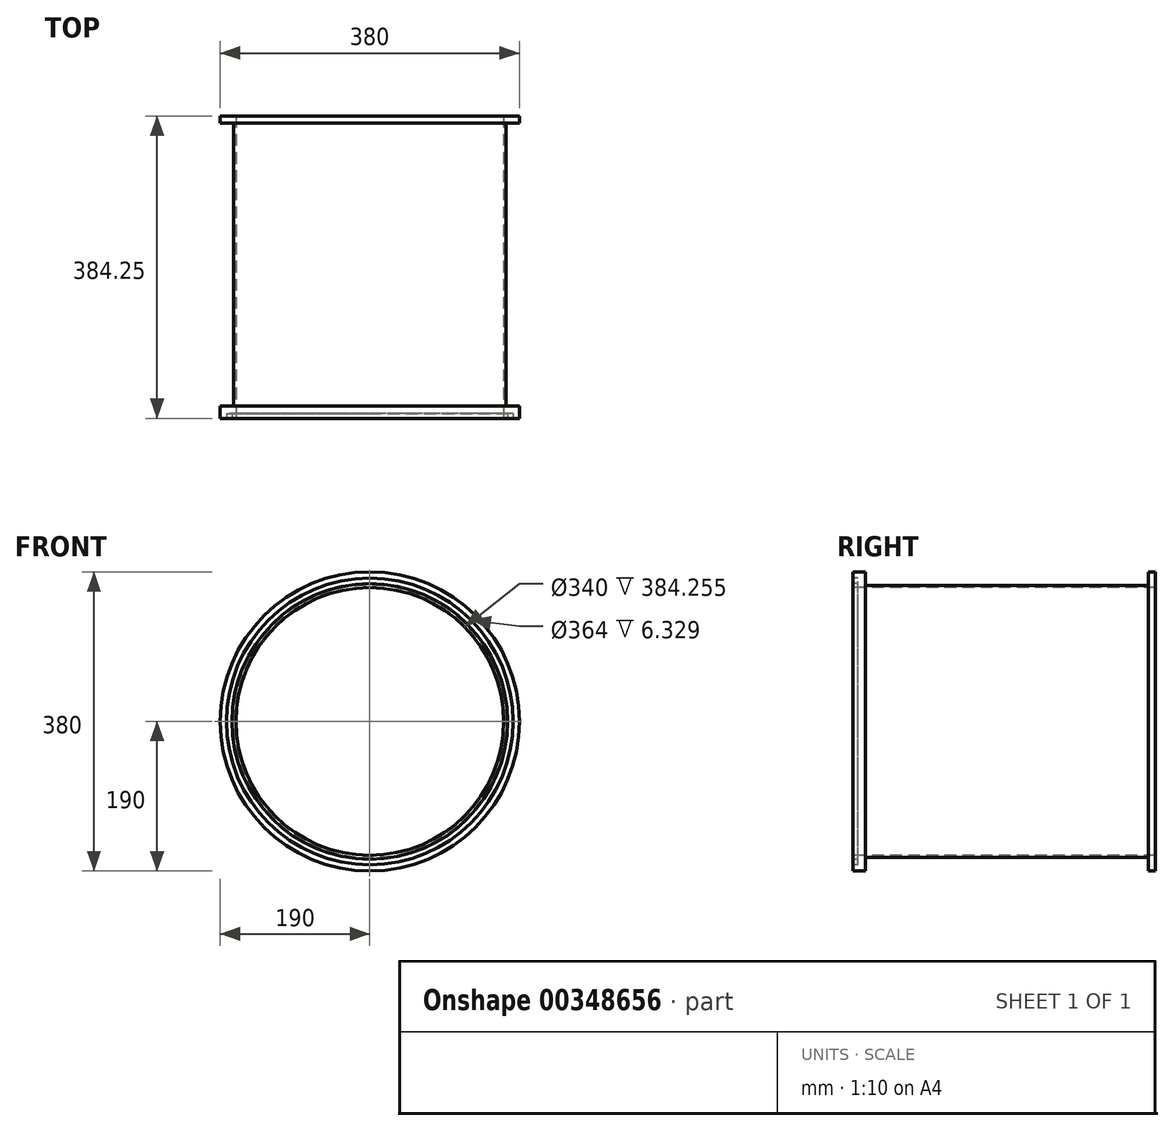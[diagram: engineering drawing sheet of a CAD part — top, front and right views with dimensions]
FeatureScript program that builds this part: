
annotation { "Feature Type Name" : "Feature", "Feature Type Description" : "" }
export const myFeature = defineFeature(function(context is Context, id is Id, definition is map)
    precondition{}
    {
        {
            var Q0;
            Q0=qCreatedBy(makeId("Right.planeOp"),FACE);
            var sketch = newSketch(context, id + "F0", { "sketchPlane" : qUnion([Q0])});
            skLineSegment(sketch, "E0.bottom", {"start": v(-1.2, 190) * mm, "end": v(14.8, 190) * mm});
            skLineSegment(sketch, "E0.top", {"start": v(-1.2, 170) * mm, "end": v(14.8, 170) * mm});
            skLineSegment(sketch, "E0.left", {"start": v(-1.2, 190) * mm, "end": v(-1.2, 182) * mm});
            skLineSegment(sketch, "E0.right", {"start": v(14.8, 190) * mm, "end": v(14.8, 170) * mm});
            skLineSegment(sketch, "E1", {"start": v(14.8, 170) * mm, "end": v(383.05, 170) * mm});
            skLineSegment(sketch, "E2.3", {"start": v(14.8, 173) * mm, "end": v(374.04, 173) * mm});
            skLineSegment(sketch, "E3.bottom", {"start": v(-1.2, 182) * mm, "end": v(5.12, 182) * mm});
            skLineSegment(sketch, "E3.top", {"start": v(-1.2, 175) * mm, "end": v(5.12, 175) * mm});
            skLineSegment(sketch, "E3.right", {"start": v(5.12, 182) * mm, "end": v(5.12, 175) * mm});
            skLineSegment(sketch, "E4.trimOffspring", {"start": v(-1.2, 175) * mm, "end": v(-1.2, 170) * mm});
            skLineSegment(sketch, "E5", {"start": v(374.04, 173) * mm, "end": v(374.04, 190) * mm});
            skLineSegment(sketch, "E6", {"start": v(374.04, 190) * mm, "end": v(383.05, 190) * mm});
            skLineSegment(sketch, "E7", {"start": v(383.05, 190) * mm, "end": v(383.05, 170) * mm});
            skPoint(sketch, "E8.orphan", {"position": v(372.56, 170) * mm});
            skLineSegment(sketch, "E9", {"start": v(0, 0) * mm, "end": v(341.36, 0) * mm});
            skSolve(sketch);
        }
        {
            var Q0;
            Q0 = qSketchRegion(id + "F0", true);
            var Q1;
            Q1=sQuery(id+"F0.wireOp",EDGE,"E9");
            revolve(context, id + "F1", {"entities" : qUnion([Q0]), "axis" : qUnion([Q1]), "revolveType" : RevolveType.FULL});
        }
    });
